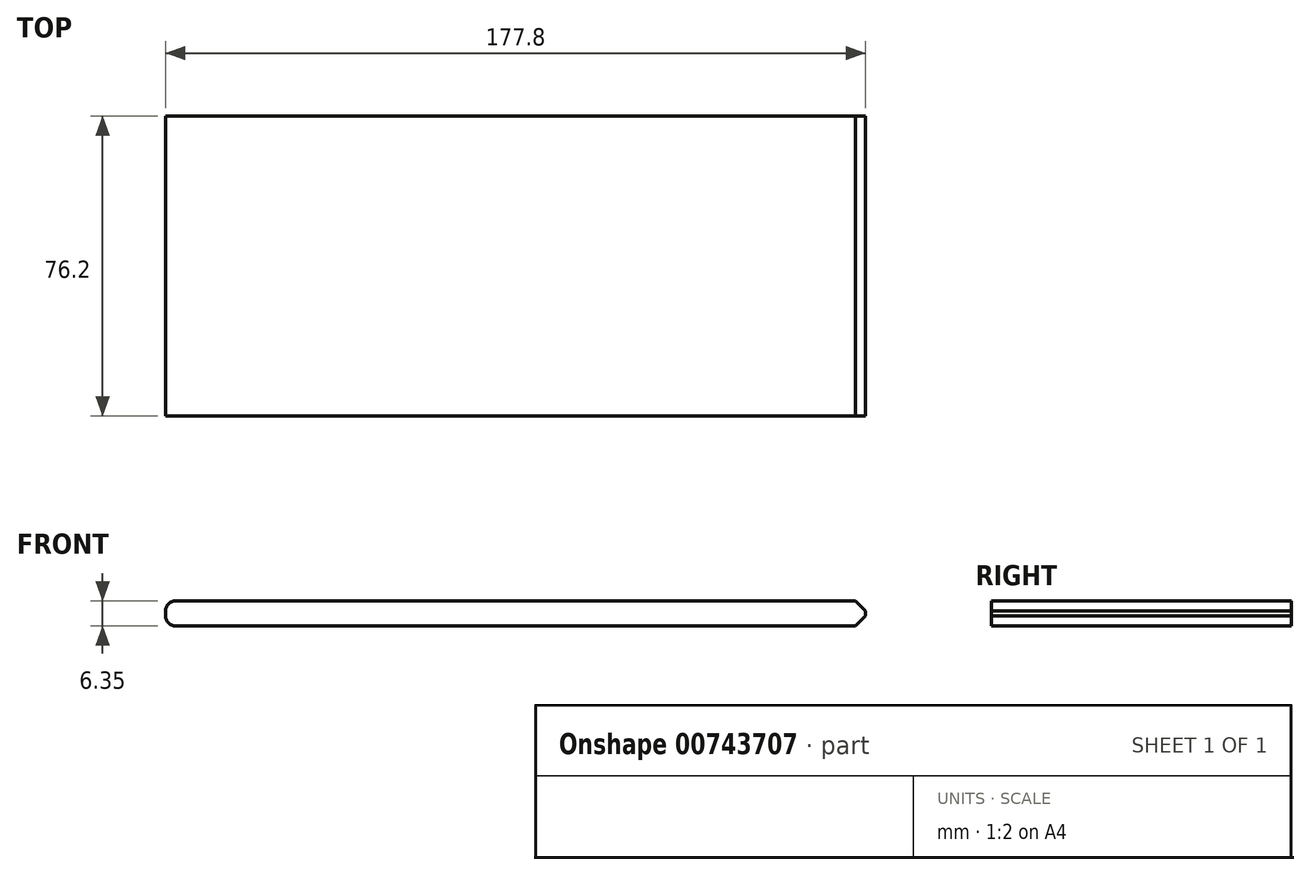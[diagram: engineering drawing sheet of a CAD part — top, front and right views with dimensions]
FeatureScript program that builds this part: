
annotation { "Feature Type Name" : "Feature", "Feature Type Description" : "" }
export const myFeature = defineFeature(function(context is Context, id is Id, definition is map)
    precondition{}
    {
        {
            var Q0;
            Q0=qCreatedBy(makeId("Top.planeOp"),FACE);
            var sketch = newSketch(context, id + "F0", { "sketchPlane" : qUnion([Q0])});
            skLineSegment(sketch, "E0.bottom", {"start": v(-81.22, -2.3) * mm, "end": v(96.58, -2.3) * mm});
            skLineSegment(sketch, "E0.top", {"start": v(-81.22, -78.5) * mm, "end": v(96.58, -78.5) * mm});
            skLineSegment(sketch, "E0.left", {"start": v(-81.22, -2.3) * mm, "end": v(-81.22, -78.5) * mm});
            skLineSegment(sketch, "E0.right", {"start": v(96.58, -2.3) * mm, "end": v(96.58, -78.5) * mm});
            skSolve(sketch);
        }
        {
            var Q0;
            Q0 = qSketchRegion(id + "F0", true);
            extrude(context, id + "F1", {"entities" : qUnion([Q0]), "depth" : 6.35 * mm, "offsetDistance" : 25.4 * mm});
        }
        {
            var Q0;
            Q0=makeQuery(id+"F1.opExtrude","CAP_EDGE",EDGE,{"disambiguationData":[OSD([sQuery(id+"F0.wireOp",EDGE,"E0.left")])],"isStart":true});
            var Q1;
            Q1=makeQuery(id+"F1.opExtrude","CAP_EDGE",EDGE,{"disambiguationData":[OSD([sQuery(id+"F0.wireOp",EDGE,"E0.left")])],"isStart":false});
            fillet(context, id + "F2", {"entities" : qUnion([Q0, Q1]), "radius" : 2.54 * mm, "tangentPropagation" : true, "allowEdgeOverflow" : false});
        }
        {
            var Q0;
            Q0=makeQuery(id+"F1.opExtrude","CAP_EDGE",EDGE,{"disambiguationData":[OSD([sQuery(id+"F0.wireOp",EDGE,"E0.right")])],"isStart":false});
            var Q1;
            Q1=makeQuery(id+"F1.opExtrude","CAP_EDGE",EDGE,{"disambiguationData":[OSD([sQuery(id+"F0.wireOp",EDGE,"E0.right")])],"isStart":true});
            chamfer(context, id + "F3", {"entities" : qUnion([Q0, Q1]), "width" : 2.54 * mm, "tangentPropagation" : true});
        }
    });
